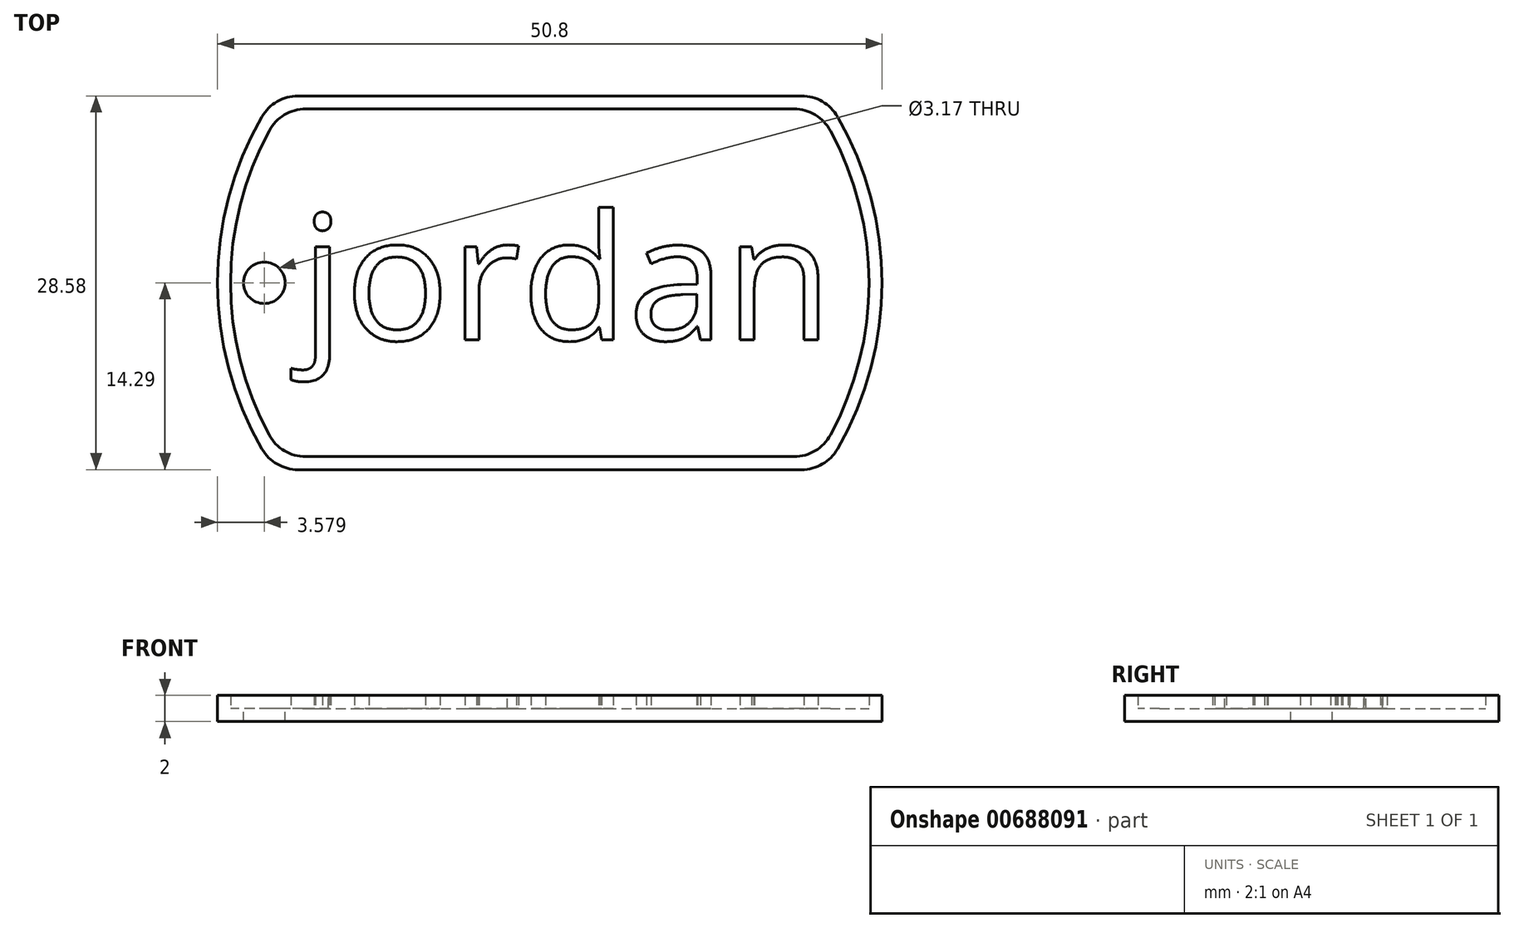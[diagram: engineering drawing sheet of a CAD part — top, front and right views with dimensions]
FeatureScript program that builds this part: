
annotation { "Feature Type Name" : "Feature", "Feature Type Description" : "" }
export const myFeature = defineFeature(function(context is Context, id is Id, definition is map)
    precondition{}
    {
        {
            var Q0;
            Q0=qCreatedBy(makeId("Top.planeOp"),FACE);
            var sketch = newSketch(context, id + "F0", { "sketchPlane" : qUnion([Q0])});
            skArc(sketch, "E0", {"start": v(-22, 12.7) * mm, "mid": v(-25.4, 0) * mm, "end": v(-22, -12.7) * mm});
            skLineSegment(sketch, "E1.top", {"start": v(-19.25, -14.29) * mm, "end": v(19.25, -14.29) * mm});
            skArc(sketch, "E2.trimOffspring", {"start": v(22, -12.7) * mm, "mid": v(25.4, 0) * mm, "end": v(22, 12.7) * mm});
            skLineSegment(sketch, "E3", {"start": v(-19.25, 14.29) * mm, "end": v(19.25, 14.29) * mm});
            skPoint(sketch, "E4.visualSharp", {"position": v(-21, 14.29) * mm});
            skArc(sketch, "E4.filletArc", {"start": v(-19.25, 14.29) * mm, "mid": v(-20.83, 13.86) * mm, "end": v(-22, 12.7) * mm});
            skPoint(sketch, "E5.visualSharp", {"position": v(21, 14.29) * mm});
            skArc(sketch, "E5.filletArc", {"start": v(22, 12.7) * mm, "mid": v(20.83, 13.86) * mm, "end": v(19.25, 14.29) * mm});
            skPoint(sketch, "E6.visualSharp", {"position": v(21, -14.29) * mm});
            skArc(sketch, "E6.filletArc", {"start": v(19.25, -14.29) * mm, "mid": v(20.83, -13.86) * mm, "end": v(22, -12.7) * mm});
            skPoint(sketch, "E7.visualSharp", {"position": v(-21, -14.29) * mm});
            skArc(sketch, "E7.filletArc", {"start": v(-22, -12.7) * mm, "mid": v(-20.83, -13.86) * mm, "end": v(-19.25, -14.29) * mm});
            skSolve(sketch);
        }
        {
            var Q0;
            Q0=makeQuery(id+"F0.imprint","IMPRINT",FACE,{"disambiguationData":[TD([[makeQuery(id+"F0.imprint","IMPRINT",EDGE,{"derivedFrom":sQuery(id+"F0.wireOp",EDGE,"E0")}),1.0]])]});
            extrude(context, id + "F1", {"entities" : qUnion([Q0]), "depth" : 1 * mm, "offsetDistance" : 25.4 * mm});
        }
        {
            var Q0;
            Q0=makeQuery(id+"F1.opExtrude","CAP_FACE",FACE,{"disambiguationData":[OSD([sQuery(id+"F0.wireOp",EDGE,"E0"),sQuery(id+"F0.wireOp",EDGE,"E1.top"),sQuery(id+"F0.wireOp",EDGE,"E2.trimOffspring"),sQuery(id+"F0.wireOp",EDGE,"E3"),sQuery(id+"F0.wireOp",EDGE,"E4.filletArc"),sQuery(id+"F0.wireOp",EDGE,"E5.filletArc"),sQuery(id+"F0.wireOp",EDGE,"E6.filletArc"),sQuery(id+"F0.wireOp",EDGE,"E7.filletArc")])],"isStart":false});
            var sketch = newSketch(context, id + "F2", { "sketchPlane" : qUnion([Q0])});
            skLineSegment(sketch, "E8.0", {"start": v(-18.66, 13.29) * mm, "end": v(18.66, 13.29) * mm});
            skArc(sketch, "E8.1", {"start": v(-21.45, 11.63) * mm, "mid": v(-24.4, 0) * mm, "end": v(-21.45, -11.63) * mm});
            skLineSegment(sketch, "E8.2", {"start": v(-18.66, -13.29) * mm, "end": v(18.66, -13.29) * mm});
            skArc(sketch, "E8.3", {"start": v(21.45, -11.63) * mm, "mid": v(24.4, 0) * mm, "end": v(21.45, 11.63) * mm});
            skPoint(sketch, "E9.visualSharp", {"position": v(-20.46, 13.29) * mm});
            skArc(sketch, "E9.filletArc", {"start": v(-18.66, 13.29) * mm, "mid": v(-20.29, 12.84) * mm, "end": v(-21.45, 11.63) * mm});
            skPoint(sketch, "E10.visualSharp", {"position": v(20.46, 13.29) * mm});
            skArc(sketch, "E10.filletArc", {"start": v(21.45, 11.63) * mm, "mid": v(20.29, 12.84) * mm, "end": v(18.66, 13.29) * mm});
            skPoint(sketch, "E11.visualSharp", {"position": v(20.46, -13.29) * mm});
            skArc(sketch, "E11.filletArc", {"start": v(18.66, -13.29) * mm, "mid": v(20.29, -12.84) * mm, "end": v(21.45, -11.63) * mm});
            skPoint(sketch, "E12.visualSharp", {"position": v(-20.46, -13.29) * mm});
            skArc(sketch, "E12.filletArc", {"start": v(-21.45, -11.63) * mm, "mid": v(-20.29, -12.84) * mm, "end": v(-18.66, -13.29) * mm});
            skLineSegment(sketch, "E13.0", {"start": v(-19.25, 14.29) * mm, "end": v(19.25, 14.29) * mm});
            skArc(sketch, "E13.1", {"start": v(-22, 12.7) * mm, "mid": v(-25.4, 0) * mm, "end": v(-22, -12.7) * mm});
            skLineSegment(sketch, "E13.2", {"start": v(-19.25, -14.29) * mm, "end": v(19.25, -14.29) * mm});
            skArc(sketch, "E13.3", {"start": v(22, -12.7) * mm, "mid": v(25.4, 0) * mm, "end": v(22, 12.7) * mm});
            skPoint(sketch, "E14.visualSharp", {"position": v(-21, -14.29) * mm});
            skArc(sketch, "E14.filletArc", {"start": v(-22, -12.7) * mm, "mid": v(-20.83, -13.86) * mm, "end": v(-19.25, -14.29) * mm});
            skPoint(sketch, "E15.visualSharp", {"position": v(21, -14.29) * mm});
            skArc(sketch, "E15.filletArc", {"start": v(19.25, -14.29) * mm, "mid": v(20.83, -13.86) * mm, "end": v(22, -12.7) * mm});
            skPoint(sketch, "E16.visualSharp", {"position": v(21, 14.29) * mm});
            skArc(sketch, "E16.filletArc", {"start": v(22, 12.7) * mm, "mid": v(20.83, 13.86) * mm, "end": v(19.25, 14.29) * mm});
            skPoint(sketch, "E17.visualSharp", {"position": v(-21, 14.29) * mm});
            skArc(sketch, "E17.filletArc", {"start": v(-19.25, 14.29) * mm, "mid": v(-20.83, 13.86) * mm, "end": v(-22, 12.7) * mm});
            skSolve(sketch);
        }
        {
            var Q0;
            Q0=makeQuery(id+"F2.imprint","IMPRINT",FACE,{"disambiguationData":[TD([[makeQuery(id+"F2.imprint","IMPRINT",EDGE,{"derivedFrom":sQuery(id+"F2.wireOp",EDGE,"E8.0")}),1.0]])]});
            extrude(context, id + "F3", {"entities" : qUnion([Q0]), "operationType" : NewBodyOperationType.ADD, "depth" : 1 * mm, "offsetDistance" : 25.4 * mm});
        }
        {
            var Q0;
            Q0=makeQuery(id+"F1.opExtrude","CAP_FACE",FACE,{"disambiguationData":[OSD([sQuery(id+"F0.wireOp",EDGE,"E0"),sQuery(id+"F0.wireOp",EDGE,"E1.top"),sQuery(id+"F0.wireOp",EDGE,"E2.trimOffspring"),sQuery(id+"F0.wireOp",EDGE,"E3"),sQuery(id+"F0.wireOp",EDGE,"E4.filletArc"),sQuery(id+"F0.wireOp",EDGE,"E5.filletArc"),sQuery(id+"F0.wireOp",EDGE,"E6.filletArc"),sQuery(id+"F0.wireOp",EDGE,"E7.filletArc")])],"isStart":false});
            var sketch = newSketch(context, id + "F4", { "sketchPlane" : qUnion([Q0])});
            skCircle(sketch, "E18", {"center": v(-21.82, 0) * mm, "radius": 1.59 * mm});
            skSolve(sketch);
        }
        {
            var Q0;
            Q0=makeQuery(id+"F4.imprint","IMPRINT",FACE,{"disambiguationData":[TD([[makeQuery(id+"F4.imprint","IMPRINT",EDGE,{"derivedFrom":sQuery(id+"F4.wireOp",EDGE,"E18")}),1.0]])]});
            extrude(context, id + "F5", {"entities" : qUnion([Q0]), "operationType" : NewBodyOperationType.REMOVE, "oppositeDirection" : true, "depth" : 1 * mm, "offsetDistance" : 25.4 * mm});
        }
        {
            var Q0;
            Q0=makeQuery(id+"F2.imprint","IMPRINT",FACE,{"disambiguationData":[TD([[makeQuery(id+"F2.imprint","IMPRINT",EDGE,{"derivedFrom":sQuery(id+"F2.wireOp",EDGE,"E8.0")}),-1.0]])]});
            var sketch = newSketch(context, id + "F6", { "sketchPlane" : qUnion([Q0])});
            skText(sketch, "E19", { "text": "jordan", "fontName": "OpenSans-Regular.ttf"});
            const initialGuessF6  = {"E19": [-0.01906, -0.00437, 1, 0, 0.0096]};
            skSetInitialGuess(sketch, initialGuessF6);
            skSolve(sketch);
        }
        {
            var Q0;
            Q0 = qSketchRegion(id + "F6", true);
            extrude(context, id + "F7", {"entities" : qUnion([Q0]), "operationType" : NewBodyOperationType.ADD, "depth" : 1 * mm, "offsetDistance" : 25.4 * mm});
        }
    });
